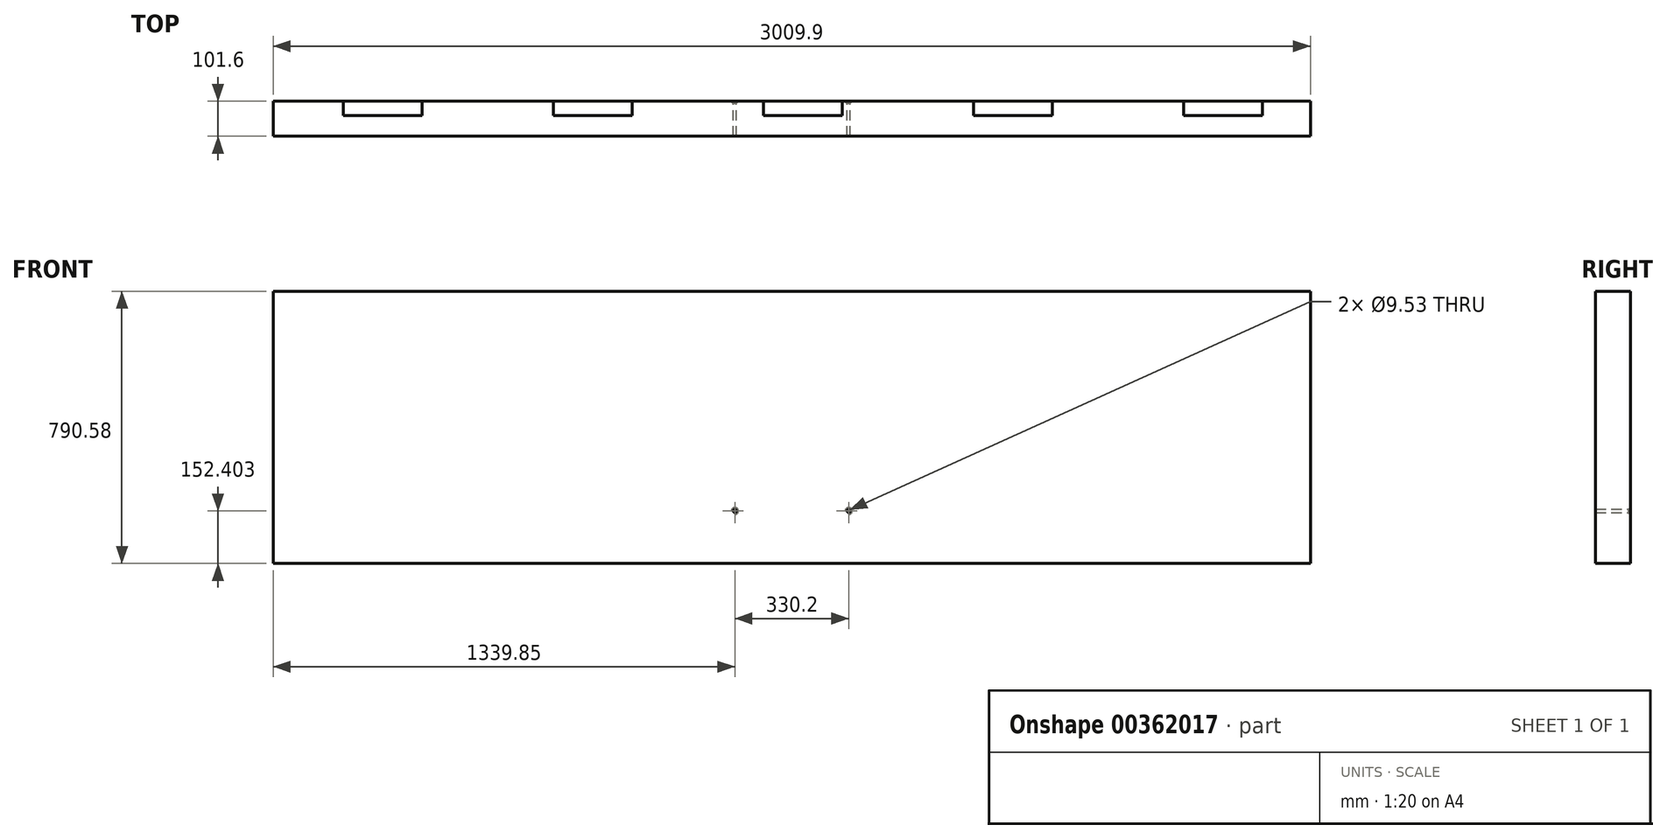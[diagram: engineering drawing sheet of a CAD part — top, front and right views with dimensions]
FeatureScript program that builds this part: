
annotation { "Feature Type Name" : "Feature", "Feature Type Description" : "" }
export const myFeature = defineFeature(function(context is Context, id is Id, definition is map)
    precondition{}
    {
        {
            var Q0;
            Q0=qCreatedBy(makeId("Front.planeOp"),FACE);
            var sketch = newSketch(context, id + "F0", { "sketchPlane" : qUnion([Q0])});
            skLineSegment(sketch, "E0.bottom", {"start": v(1504.95, -395.29) * mm, "end": v(-1504.95, -395.29) * mm});
            skLineSegment(sketch, "E0.top", {"start": v(1504.95, 395.29) * mm, "end": v(-1504.95, 395.29) * mm});
            skLineSegment(sketch, "E0.left", {"start": v(1504.95, -395.29) * mm, "end": v(1504.95, 395.29) * mm});
            skLineSegment(sketch, "E0.right", {"start": v(-1504.95, -395.29) * mm, "end": v(-1504.95, 395.29) * mm});
            skPoint(sketch, "E0.middle", {"position": v(0, 0) * mm});
            skSolve(sketch);
        }
        {
            var Q0;
            Q0=makeQuery(id+"F0.imprint","IMPRINT",FACE,{"disambiguationData":[TD([[makeQuery(id+"F0.imprint","IMPRINT",EDGE,{"derivedFrom":sQuery(id+"F0.wireOp",EDGE,"E0.bottom")}),-1.0]])]});
            extrude(context, id + "F1", {"entities" : qUnion([Q0]), "depth" : 101.6 * mm});
        }
        {
            var Q0;
            Q0=makeQuery(id+"F1.opExtrude","SWEPT_FACE",FACE,{"disambiguationData":[OSD([sQuery(id+"F0.wireOp",EDGE,"E0.top")])]});
            var sketch = newSketch(context, id + "F2", { "sketchPlane" : qUnion([Q0])});
            skLineSegment(sketch, "E1.bottom", {"start": v(-1301.75, 0) * mm, "end": v(-1073.15, 0) * mm});
            skLineSegment(sketch, "E1.top", {"start": v(-1301.75, -41.9) * mm, "end": v(-1073.15, -41.9) * mm});
            skLineSegment(sketch, "E1.left", {"start": v(-1301.75, 0) * mm, "end": v(-1301.75, -41.9) * mm});
            skLineSegment(sketch, "E1.right", {"start": v(-1073.15, 0) * mm, "end": v(-1073.15, -41.9) * mm});
            skLineSegment(sketch, "E2.bottom", {"start": v(-692.15, 0) * mm, "end": v(-463.55, 0) * mm});
            skLineSegment(sketch, "E2.top", {"start": v(-692.15, -41.9) * mm, "end": v(-463.55, -41.9) * mm});
            skLineSegment(sketch, "E2.left", {"start": v(-692.15, 0) * mm, "end": v(-692.15, -41.9) * mm});
            skLineSegment(sketch, "E2.right", {"start": v(-463.55, 0) * mm, "end": v(-463.55, -41.9) * mm});
            skLineSegment(sketch, "E3.bottom", {"start": v(-82.55, 0) * mm, "end": v(146.05, 0) * mm});
            skLineSegment(sketch, "E3.top", {"start": v(-82.55, -41.9) * mm, "end": v(146.05, -41.9) * mm});
            skLineSegment(sketch, "E3.left", {"start": v(-82.55, 0) * mm, "end": v(-82.55, -41.9) * mm});
            skLineSegment(sketch, "E3.right", {"start": v(146.05, 0) * mm, "end": v(146.05, -41.9) * mm});
            skLineSegment(sketch, "E4.bottom", {"start": v(527.05, 0) * mm, "end": v(755.65, 0) * mm});
            skLineSegment(sketch, "E4.top", {"start": v(527.05, -41.9) * mm, "end": v(755.65, -41.9) * mm});
            skLineSegment(sketch, "E4.left", {"start": v(527.05, 0) * mm, "end": v(527.05, -41.9) * mm});
            skLineSegment(sketch, "E4.right", {"start": v(755.65, 0) * mm, "end": v(755.65, -41.9) * mm});
            skLineSegment(sketch, "E5.bottom", {"start": v(1136.65, 0) * mm, "end": v(1365.25, 0) * mm});
            skLineSegment(sketch, "E5.top", {"start": v(1136.65, -41.9) * mm, "end": v(1365.25, -41.9) * mm});
            skLineSegment(sketch, "E5.left", {"start": v(1136.65, 0) * mm, "end": v(1136.65, -41.9) * mm});
            skLineSegment(sketch, "E5.right", {"start": v(1365.25, 0) * mm, "end": v(1365.25, -41.9) * mm});
            skSolve(sketch);
        }
        {
            var Q0;
            Q0 = qSketchRegion(id + "F2", true);
            extrude(context, id + "F3", {"entities" : qUnion([Q0]), "operationType" : NewBodyOperationType.REMOVE, "oppositeDirection" : true, "depth" : 3.17 * mm});
        }
        {
            var Q0;
            Q0=makeQuery(id+"F1.opExtrude","CAP_FACE",FACE,{"disambiguationData":[OSD([sQuery(id+"F0.wireOp",EDGE,"E0.bottom"),sQuery(id+"F0.wireOp",EDGE,"E0.top"),sQuery(id+"F0.wireOp",EDGE,"E0.left"),sQuery(id+"F0.wireOp",EDGE,"E0.right")])],"isStart":true});
            var sketch = newSketch(context, id + "F4", { "sketchPlane" : qUnion([Q0])});
            skPoint(sketch, "E6", {"position": v(-165.1, -242.89) * mm});
            skPoint(sketch, "E7.MirrorP", {"position": v(165.1, -242.89) * mm});
            skSolve(sketch);
        }
        {
            var Q0;
            Q0=sQuery(id+"F4.wireOp",VERTEX,"E6");
            var Q1;
            Q1=sQuery(id+"F4.wireOp",VERTEX,"E7.MirrorP");
            var Q2;
            Q2=makeQuery(id+"F1.opExtrude","SWEPT_BODY",BODY,{"disambiguationData":[OSD([sQuery(id+"F0.wireOp",EDGE,"E0.bottom"),sQuery(id+"F0.wireOp",EDGE,"E0.top"),sQuery(id+"F0.wireOp",EDGE,"E0.left"),sQuery(id+"F0.wireOp",EDGE,"E0.right")])]});
            hole(context, id + "F5", {"style" : HoleStyle.C_SINK, "endStyle" : HoleEndStyle.THROUGH, "holeDiameter" : 9.52 * mm, "cSinkDiameter" : 19.84 * mm, "cSinkAngle" : 82 * degree, "isTappedThrough" : true, "tappedDepth" : 12.7 * mm, "tapClearance" : 3, "locations" : qUnion([Q0, Q1]), "scope" : qUnion([Q2])});
        }
    });
